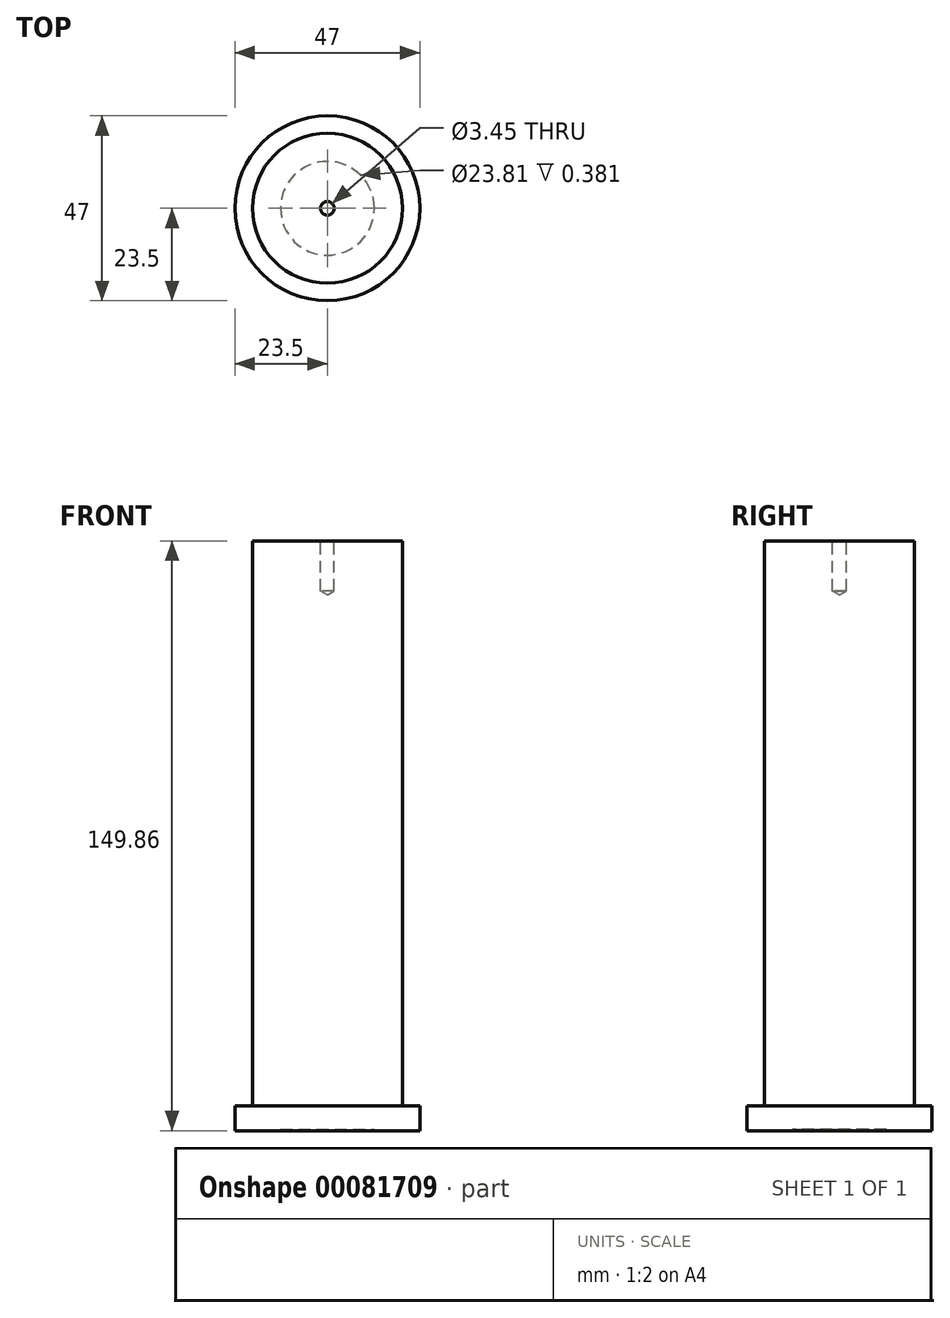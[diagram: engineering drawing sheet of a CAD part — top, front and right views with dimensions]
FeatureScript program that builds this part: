
annotation { "Feature Type Name" : "Feature", "Feature Type Description" : "" }
export const myFeature = defineFeature(function(context is Context, id is Id, definition is map)
    precondition{}
    {
        {
            var Q0;
            Q0=qCreatedBy(makeId("Top.planeOp"),FACE);
            var sketch = newSketch(context, id + "F0", { "sketchPlane" : qUnion([Q0])});
            skCircle(sketch, "E0", {"center": v(0, 0) * mm, "radius": 23.5 * mm});
            skCircle(sketch, "E1", {"center": v(0, 0) * mm, "radius": 19.05 * mm});
            skSolve(sketch);
        }
        {
            var Q0;
            Q0=makeQuery(id+"F0.imprint","IMPRINT",FACE,{"disambiguationData":[TD([[makeQuery(id+"F0.imprint","IMPRINT",EDGE,{"derivedFrom":sQuery(id+"F0.wireOp",EDGE,"E0")}),1.0]])]});
            extrude(context, id + "F1", {"entities" : qUnion([Q0]), "depth" : 6.35 * mm});
        }
        {
            var Q0;
            Q0=makeQuery(id+"F0.imprint","IMPRINT",FACE,{"disambiguationData":[TD([[makeQuery(id+"F0.imprint","IMPRINT",EDGE,{"derivedFrom":sQuery(id+"F0.wireOp",EDGE,"E1")}),1.0]])]});
            extrude(context, id + "F2", {"entities" : qUnion([Q0]), "operationType" : NewBodyOperationType.ADD, "depth" : 149.86 * mm});
        }
        {
            var Q0;
            Q0=makeQuery(id+"F2.opExtrude","CAP_FACE",FACE,{"disambiguationData":[OSD([sQuery(id+"F0.wireOp",EDGE,"E1")])],"isStart":false});
            var sketch = newSketch(context, id + "F3", { "sketchPlane" : qUnion([Q0])});
            skPoint(sketch, "E2", {"position": v(0, 0) * mm});
            skSolve(sketch);
        }
        {
            var Q0;
            Q0=sQuery(id+"F3.wireOp",VERTEX,"E2");
            var Q1;
            Q1=makeQuery(id+"F1.opExtrude","SWEPT_BODY",BODY,{"disambiguationData":[OSD([sQuery(id+"F0.wireOp",EDGE,"E0"),sQuery(id+"F0.wireOp",EDGE,"E1")])]});
            hole(context, id + "F4", {"style" : HoleStyle.SIMPLE, "endStyle" : HoleEndStyle.BLIND, "standardTappedOrClearance" : lookupTablePath({ "standard" : "ANSI", "engagement" : "75%", "pitch" : "32 tpi", "size" : "#8", "type" : "Tapped" }), "standardBlindInLast" : lookupTablePath({ "standard" : "ANSI", "engagement" : "75%", "pitch" : "32 tpi", "size" : "#8", "type" : "Tapped" }), "holeDiameter" : 3.45 * mm, "holeDepth" : 12.7 * mm, "locations" : qUnion([Q0]), "scope" : qUnion([Q1]), "majorDiameter" : 4.17 * mm});
        }
        {
            var Q0;
            Q0=makeQuery(id+"F1.opExtrude","SWEPT_BODY",BODY,{"disambiguationData":[OSD([sQuery(id+"F0.wireOp",EDGE,"E0"),sQuery(id+"F0.wireOp",EDGE,"E1")])]});
            transform(context, id + "F5", {"entities" : qUnion([Q0]), "transformType" : TransformType.TRANSLATION_3D, "dx" : 0 * mm, "dy" : 0 * mm, "dz" : 0 * mm, "makeCopy" : true});
        }
        {
            var Q0;
            Q0=makeQuery(id+"F5.opPattern","COPY",BODY,{"derivedFrom":makeQuery(id+"F1.opExtrude","SWEPT_BODY",BODY,{"disambiguationData":[OSD([sQuery(id+"F0.wireOp",EDGE,"E0"),sQuery(id+"F0.wireOp",EDGE,"E1")])]}),"instanceName":"1"});
            deleteBodies(context, id + "F6", {"entities" : qUnion([Q0])});
        }
        {
            var Q0;
            {var subQ0=sQuery(id+"F0.wireOp",EDGE,"E1");Q0=makeQuery(id+"F2.boolean.opBoolean","MERGE",FACE,{"derivedFrom":[makeQuery(id+"F1.opExtrude","CAP_FACE",FACE,{"disambiguationData":[OSD([sQuery(id+"F0.wireOp",EDGE,"E0"),subQ0])],"isStart":true}),makeQuery(id+"F2.opExtrude","CAP_FACE",FACE,{"disambiguationData":[OSD([subQ0])],"isStart":true})]});}
            var sketch = newSketch(context, id + "F7", { "sketchPlane" : qUnion([Q0])});
            skCircle(sketch, "E3", {"center": v(0, 0) * mm, "radius": 11.9 * mm});
            skSolve(sketch);
        }
        {
            var Q0;
            Q0 = qSketchRegion(id + "F7", true);
            extrude(context, id + "F8", {"entities" : qUnion([Q0]), "operationType" : NewBodyOperationType.REMOVE, "oppositeDirection" : true, "depth" : 0.38 * mm});
        }
    });
